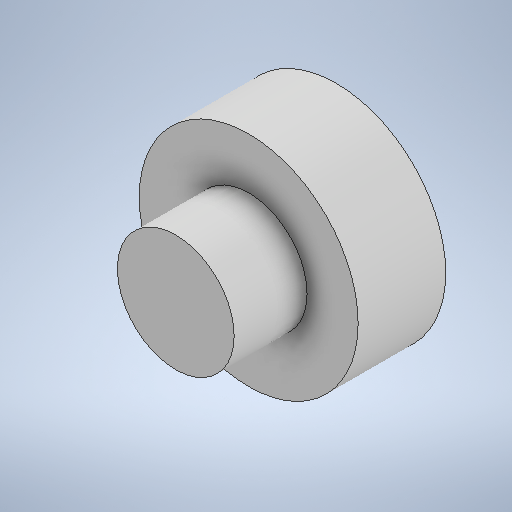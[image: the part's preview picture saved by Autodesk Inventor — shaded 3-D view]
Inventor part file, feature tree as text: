
AUTODESK INVENTOR PART (.ipt)
format: ipt  version: 2025.1 (Build 291241000, 241)  size: 247,296 bytes
history: native  units: mm
features: sketch x2, revolve x1, hole x1
ambient origin geometry x8: Origin, YZ Plane, XZ Plane, XY Plane, X Axis, Y Axis, Z Axis, Center Point
bodies: Solid1 (feature_tree)
feature tree (4):
  revolve  "Revolution1"  [1 undecoded]
  hole  "Hole1"  [1 undecoded]
  sketch  "Sketch1"  dims[d0=8.0mm d1=15.0mm]
  sketch  "Sketch2"  dims[d2=5.0mm d3=6.0mm d4=90.0deg d5=6.647mm d6=6.0mm d7=4.0mm d8=2.0mm d9=90.0deg d10=6.0mm d11=0.0mm]
note: 2 required parameter values undecoded (feature->parameter linkage not recoverable at this tier; creation-order binding heuristic only, values carry confidence <= 0.55)